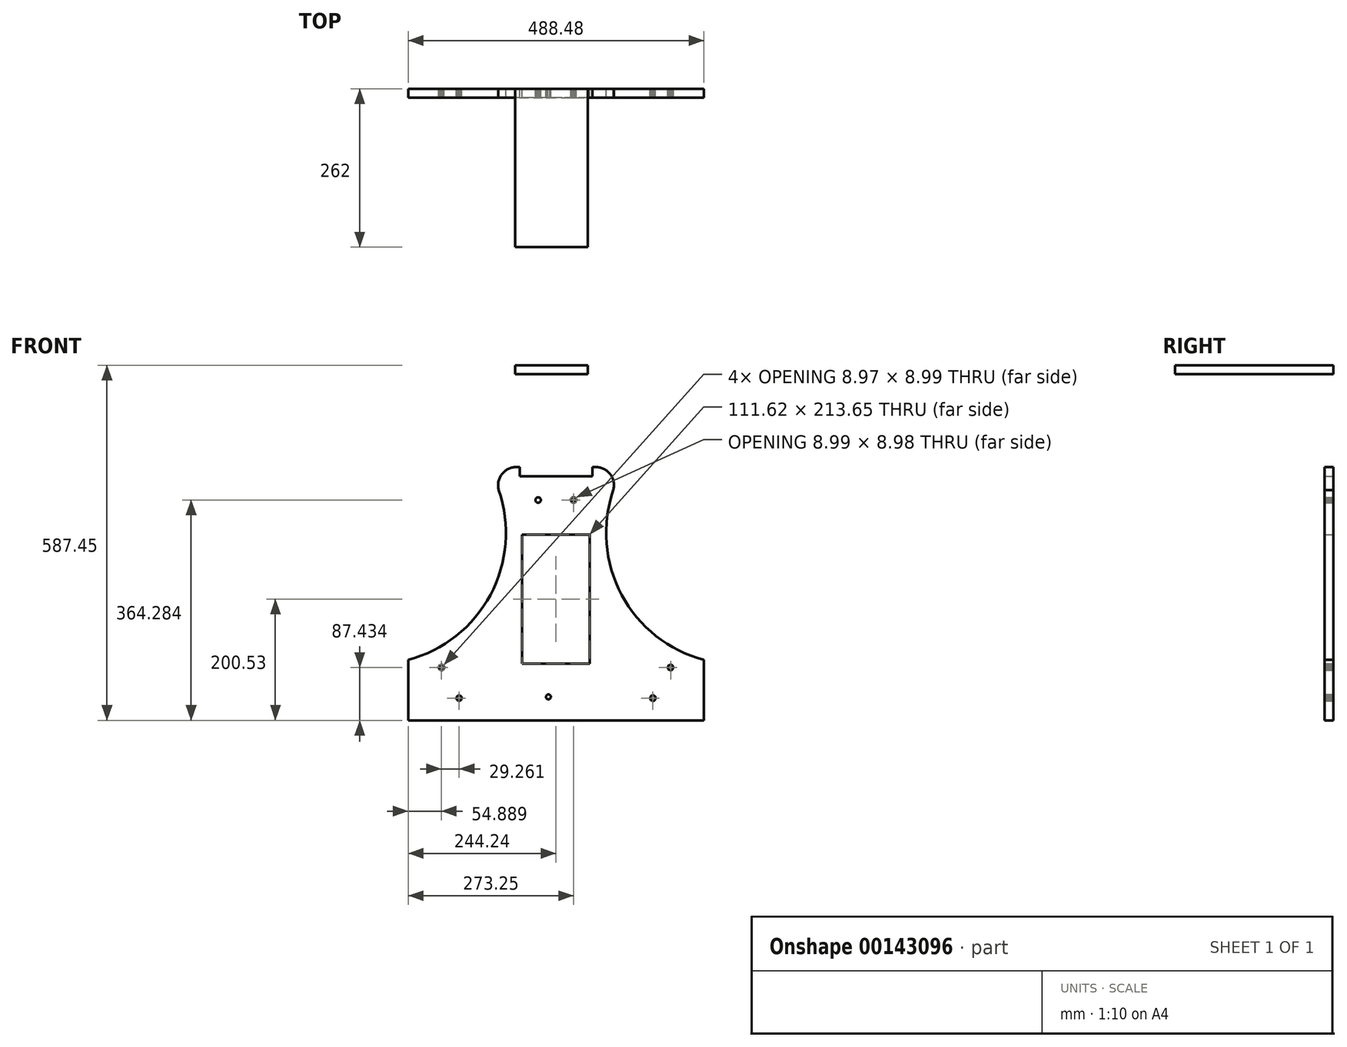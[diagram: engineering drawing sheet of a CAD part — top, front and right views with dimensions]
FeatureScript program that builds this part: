
annotation { "Feature Type Name" : "Feature", "Feature Type Description" : "" }
export const myFeature = defineFeature(function(context is Context, id is Id, definition is map)
    precondition{}
    {
        {
            var Q0;
            Q0=qCreatedBy(makeId("Front.planeOp"),FACE);
            var sketch = newSketch(context, id + "F0", { "sketchPlane" : qUnion([Q0])});
            skLineSegment(sketch, "E0", {"start": v(-16.38, -155.1) * mm, "end": v(-13.24, -155.1) * mm});
            skLineSegment(sketch, "E1", {"start": v(-13.24, -155.1) * mm, "end": v(-12.29, -155.09) * mm});
            skLineSegment(sketch, "E2", {"start": v(-12.29, -155.09) * mm, "end": v(-12.29, -155.23) * mm});
            skLineSegment(sketch, "E3", {"start": v(-12.29, -155.23) * mm, "end": v(-15.24, -155.23) * mm});
            skLineSegment(sketch, "E4", {"start": v(-15.24, -155.23) * mm, "end": v(-15.24, -158.33) * mm});
            skLineSegment(sketch, "E5", {"start": v(-15.24, -158.33) * mm, "end": v(-15.86, -159) * mm});
            skLineSegment(sketch, "E6", {"start": v(-15.86, -159) * mm, "end": v(-16.32, -159.79) * mm});
            skLineSegment(sketch, "E7", {"start": v(-16.32, -159.79) * mm, "end": v(-16.6, -160.66) * mm});
            skLineSegment(sketch, "E8", {"start": v(-16.6, -160.66) * mm, "end": v(-16.69, -161.56) * mm});
            skLineSegment(sketch, "E9", {"start": v(-16.69, -161.56) * mm, "end": v(-16.58, -162.47) * mm});
            skLineSegment(sketch, "E10", {"start": v(-16.58, -162.47) * mm, "end": v(-16.27, -163.33) * mm});
            skLineSegment(sketch, "E11", {"start": v(-16.27, -163.33) * mm, "end": v(-15.79, -164.1) * mm});
            skLineSegment(sketch, "E12", {"start": v(-15.79, -164.1) * mm, "end": v(-15.15, -164.75) * mm});
            skLineSegment(sketch, "E13", {"start": v(-15.15, -164.75) * mm, "end": v(-14.39, -165.25) * mm});
            skLineSegment(sketch, "E14", {"start": v(-14.39, -165.25) * mm, "end": v(-13.54, -165.57) * mm});
            skLineSegment(sketch, "E15", {"start": v(-13.54, -165.57) * mm, "end": v(-12.63, -165.7) * mm});
            skLineSegment(sketch, "E16", {"start": v(-12.63, -165.7) * mm, "end": v(-11.72, -165.64) * mm});
            skLineSegment(sketch, "E17", {"start": v(-11.72, -165.64) * mm, "end": v(-10.85, -165.37) * mm});
            skLineSegment(sketch, "E18", {"start": v(-10.85, -165.37) * mm, "end": v(-10.05, -164.93) * mm});
            skLineSegment(sketch, "E19", {"start": v(-10.05, -164.93) * mm, "end": v(-9.37, -164.32) * mm});
            skLineSegment(sketch, "E20", {"start": v(-9.37, -164.32) * mm, "end": v(-8.84, -163.59) * mm});
            skLineSegment(sketch, "E21", {"start": v(-8.84, -163.59) * mm, "end": v(-8.48, -162.75) * mm});
            skLineSegment(sketch, "E22", {"start": v(-8.48, -162.75) * mm, "end": v(-8.3, -161.85) * mm});
            skLineSegment(sketch, "E23", {"start": v(-8.3, -161.85) * mm, "end": v(-8.33, -160.94) * mm});
            skLineSegment(sketch, "E24", {"start": v(-8.33, -160.94) * mm, "end": v(-8.55, -160.06) * mm});
            skLineSegment(sketch, "E25", {"start": v(-8.55, -160.06) * mm, "end": v(-8.95, -159.24) * mm});
            skLineSegment(sketch, "E26", {"start": v(-8.95, -159.24) * mm, "end": v(-9.53, -158.53) * mm});
            skLineSegment(sketch, "E27", {"start": v(-9.53, -158.53) * mm, "end": v(-10.24, -157.96) * mm});
            skLineSegment(sketch, "E28", {"start": v(-10.24, -157.96) * mm, "end": v(-10.24, -155.1) * mm});
            skLineSegment(sketch, "E29", {"start": v(-10.24, -155.1) * mm, "end": v(-6.14, -155.1) * mm});
            skLineSegment(sketch, "E30", {"start": v(-161.28, -168.1) * mm, "end": v(-160.32, -168.25) * mm});
            skLineSegment(sketch, "E31", {"start": v(-160.32, -168.25) * mm, "end": v(-159.35, -168.2) * mm});
            skLineSegment(sketch, "E32", {"start": v(-159.35, -168.2) * mm, "end": v(-158.41, -167.94) * mm});
            skLineSegment(sketch, "E33", {"start": v(-158.41, -167.94) * mm, "end": v(-158.38, -167.92) * mm});
            skLineSegment(sketch, "E34", {"start": v(-158.38, -167.92) * mm, "end": v(-157.55, -167.48) * mm});
            skLineSegment(sketch, "E35", {"start": v(-157.55, -167.48) * mm, "end": v(-156.8, -166.85) * mm});
            skLineSegment(sketch, "E36", {"start": v(-156.8, -166.85) * mm, "end": v(-156.22, -166.08) * mm});
            skLineSegment(sketch, "E37", {"start": v(-156.22, -166.08) * mm, "end": v(-155.81, -165.2) * mm});
            skLineSegment(sketch, "E38", {"start": v(-155.81, -165.2) * mm, "end": v(-155.6, -164.24) * mm});
            skLineSegment(sketch, "E39", {"start": v(-155.6, -164.24) * mm, "end": v(-155.6, -163.27) * mm});
            skLineSegment(sketch, "E40", {"start": v(-155.6, -163.27) * mm, "end": v(-155.81, -162.32) * mm});
            skLineSegment(sketch, "E41", {"start": v(-155.81, -162.32) * mm, "end": v(-156.22, -161.44) * mm});
            skLineSegment(sketch, "E42", {"start": v(-156.22, -161.44) * mm, "end": v(-156.8, -160.66) * mm});
            skLineSegment(sketch, "E43", {"start": v(-156.8, -160.66) * mm, "end": v(-157.55, -160.03) * mm});
            skLineSegment(sketch, "E44", {"start": v(-157.55, -160.03) * mm, "end": v(-158.41, -159.58) * mm});
            skLineSegment(sketch, "E45", {"start": v(-158.41, -159.58) * mm, "end": v(-159.35, -159.32) * mm});
            skLineSegment(sketch, "E46", {"start": v(-159.35, -159.32) * mm, "end": v(-160.32, -159.26) * mm});
            skLineSegment(sketch, "E47", {"start": v(-160.32, -159.26) * mm, "end": v(-161.28, -159.42) * mm});
            skLineSegment(sketch, "E48", {"start": v(-161.28, -159.42) * mm, "end": v(-162.18, -159.78) * mm});
            skLineSegment(sketch, "E49", {"start": v(-162.18, -159.78) * mm, "end": v(-163, -160.33) * mm});
            skLineSegment(sketch, "E50", {"start": v(-163, -160.33) * mm, "end": v(-163.66, -161.04) * mm});
            skLineSegment(sketch, "E51", {"start": v(-163.66, -161.04) * mm, "end": v(-164.16, -161.87) * mm});
            skLineSegment(sketch, "E52", {"start": v(-164.16, -161.87) * mm, "end": v(-164.47, -162.8) * mm});
            skLineSegment(sketch, "E53", {"start": v(-164.47, -162.8) * mm, "end": v(-164.58, -163.76) * mm});
            skLineSegment(sketch, "E54", {"start": v(-164.58, -163.76) * mm, "end": v(-164.47, -164.73) * mm});
            skLineSegment(sketch, "E55", {"start": v(-164.47, -164.73) * mm, "end": v(-164.16, -165.65) * mm});
            skLineSegment(sketch, "E56", {"start": v(-164.16, -165.65) * mm, "end": v(-163.66, -166.48) * mm});
            skLineSegment(sketch, "E57", {"start": v(-163.66, -166.48) * mm, "end": v(-163, -167.19) * mm});
            skLineSegment(sketch, "E58", {"start": v(-163, -167.19) * mm, "end": v(-162.18, -167.73) * mm});
            skLineSegment(sketch, "E59", {"start": v(-162.18, -167.73) * mm, "end": v(-161.28, -168.1) * mm});
            skLineSegment(sketch, "E60", {"start": v(185.48, -115.42) * mm, "end": v(186.07, -116.2) * mm});
            skLineSegment(sketch, "E61", {"start": v(186.07, -116.2) * mm, "end": v(186.81, -116.82) * mm});
            skLineSegment(sketch, "E62", {"start": v(186.81, -116.82) * mm, "end": v(187.67, -117.28) * mm});
            skLineSegment(sketch, "E63", {"start": v(187.67, -117.28) * mm, "end": v(188.6, -117.54) * mm});
            skLineSegment(sketch, "E64", {"start": v(188.6, -117.54) * mm, "end": v(189.58, -117.59) * mm});
            skLineSegment(sketch, "E65", {"start": v(189.58, -117.59) * mm, "end": v(190.54, -117.43) * mm});
            skLineSegment(sketch, "E66", {"start": v(190.54, -117.43) * mm, "end": v(191.45, -117.07) * mm});
            skLineSegment(sketch, "E67", {"start": v(191.45, -117.07) * mm, "end": v(192.25, -116.53) * mm});
            skLineSegment(sketch, "E68", {"start": v(192.25, -116.53) * mm, "end": v(192.92, -115.82) * mm});
            skLineSegment(sketch, "E69", {"start": v(192.92, -115.82) * mm, "end": v(193.42, -114.99) * mm});
            skLineSegment(sketch, "E70", {"start": v(193.42, -114.99) * mm, "end": v(193.73, -114.06) * mm});
            skLineSegment(sketch, "E71", {"start": v(193.73, -114.06) * mm, "end": v(193.84, -113.1) * mm});
            skLineSegment(sketch, "E72", {"start": v(193.84, -113.1) * mm, "end": v(193.73, -112.13) * mm});
            skLineSegment(sketch, "E73", {"start": v(193.73, -112.13) * mm, "end": v(193.42, -111.2) * mm});
            skLineSegment(sketch, "E74", {"start": v(193.42, -111.2) * mm, "end": v(192.92, -110.37) * mm});
            skLineSegment(sketch, "E75", {"start": v(192.92, -110.37) * mm, "end": v(192.25, -109.67) * mm});
            skLineSegment(sketch, "E76", {"start": v(192.25, -109.67) * mm, "end": v(191.45, -109.12) * mm});
            skLineSegment(sketch, "E77", {"start": v(191.45, -109.12) * mm, "end": v(190.54, -108.76) * mm});
            skLineSegment(sketch, "E78", {"start": v(190.54, -108.76) * mm, "end": v(189.58, -108.6) * mm});
            skLineSegment(sketch, "E79", {"start": v(189.58, -108.6) * mm, "end": v(188.6, -108.65) * mm});
            skLineSegment(sketch, "E80", {"start": v(188.6, -108.65) * mm, "end": v(187.67, -108.92) * mm});
            skLineSegment(sketch, "E81", {"start": v(187.67, -108.92) * mm, "end": v(186.81, -109.37) * mm});
            skLineSegment(sketch, "E82", {"start": v(186.81, -109.37) * mm, "end": v(186.07, -110) * mm});
            skLineSegment(sketch, "E83", {"start": v(186.07, -110) * mm, "end": v(185.48, -110.78) * mm});
            skLineSegment(sketch, "E84", {"start": v(185.48, -110.78) * mm, "end": v(185.07, -111.66) * mm});
            skLineSegment(sketch, "E85", {"start": v(185.07, -111.66) * mm, "end": v(184.86, -112.6) * mm});
            skLineSegment(sketch, "E86", {"start": v(184.86, -112.6) * mm, "end": v(184.86, -113.58) * mm});
            skLineSegment(sketch, "E87", {"start": v(184.86, -113.58) * mm, "end": v(185.07, -114.53) * mm});
            skLineSegment(sketch, "E88", {"start": v(185.07, -114.53) * mm, "end": v(185.48, -115.42) * mm});
            skLineSegment(sketch, "E89", {"start": v(-30.85, 168.06) * mm, "end": v(-31.74, 167.67) * mm});
            skLineSegment(sketch, "E90", {"start": v(-31.74, 167.67) * mm, "end": v(-32.53, 167.1) * mm});
            skLineSegment(sketch, "E91", {"start": v(-32.53, 167.1) * mm, "end": v(-33.17, 166.36) * mm});
            skLineSegment(sketch, "E92", {"start": v(-33.17, 166.36) * mm, "end": v(-33.64, 165.51) * mm});
            skLineSegment(sketch, "E93", {"start": v(-33.64, 165.51) * mm, "end": v(-33.92, 164.58) * mm});
            skLineSegment(sketch, "E94", {"start": v(-33.92, 164.58) * mm, "end": v(-33.99, 163.6) * mm});
            skLineSegment(sketch, "E95", {"start": v(-33.99, 163.6) * mm, "end": v(-33.85, 162.65) * mm});
            skLineSegment(sketch, "E96", {"start": v(-33.85, 162.65) * mm, "end": v(-33.5, 161.73) * mm});
            skLineSegment(sketch, "E97", {"start": v(-33.5, 161.73) * mm, "end": v(-32.97, 160.92) * mm});
            skLineSegment(sketch, "E98", {"start": v(-32.97, 160.92) * mm, "end": v(-32.28, 160.24) * mm});
            skLineSegment(sketch, "E99", {"start": v(-32.28, 160.24) * mm, "end": v(-31.45, 159.72) * mm});
            skLineSegment(sketch, "E100", {"start": v(-31.45, 159.72) * mm, "end": v(-30.54, 159.4) * mm});
            skLineSegment(sketch, "E101", {"start": v(-30.54, 159.4) * mm, "end": v(-29.57, 159.27) * mm});
            skLineSegment(sketch, "E102", {"start": v(-29.57, 159.27) * mm, "end": v(-28.6, 159.36) * mm});
            skLineSegment(sketch, "E103", {"start": v(-28.6, 159.36) * mm, "end": v(-27.68, 159.65) * mm});
            skLineSegment(sketch, "E104", {"start": v(-27.68, 159.65) * mm, "end": v(-26.83, 160.14) * mm});
            skLineSegment(sketch, "E105", {"start": v(-26.83, 160.14) * mm, "end": v(-26.12, 160.8) * mm});
            skLineSegment(sketch, "E106", {"start": v(-26.12, 160.8) * mm, "end": v(-25.56, 161.6) * mm});
            skLineSegment(sketch, "E107", {"start": v(-25.56, 161.6) * mm, "end": v(-25.18, 162.49) * mm});
            skLineSegment(sketch, "E108", {"start": v(-25.18, 162.49) * mm, "end": v(-25, 163.45) * mm});
            skLineSegment(sketch, "E109", {"start": v(-25, 163.45) * mm, "end": v(-25.04, 164.42) * mm});
            skLineSegment(sketch, "E110", {"start": v(-25.04, 164.42) * mm, "end": v(-25.28, 165.36) * mm});
            skLineSegment(sketch, "E111", {"start": v(-25.28, 165.36) * mm, "end": v(-25.72, 166.23) * mm});
            skLineSegment(sketch, "E112", {"start": v(-25.72, 166.23) * mm, "end": v(-26.34, 166.98) * mm});
            skLineSegment(sketch, "E113", {"start": v(-26.34, 166.98) * mm, "end": v(-27.1, 167.58) * mm});
            skLineSegment(sketch, "E114", {"start": v(-27.1, 167.58) * mm, "end": v(-27.98, 168) * mm});
            skLineSegment(sketch, "E115", {"start": v(-27.98, 168) * mm, "end": v(-28.92, 168.23) * mm});
            skLineSegment(sketch, "E116", {"start": v(-28.92, 168.23) * mm, "end": v(-29.9, 168.25) * mm});
            skLineSegment(sketch, "E117", {"start": v(-29.9, 168.25) * mm, "end": v(-30.85, 168.06) * mm});
            skLineSegment(sketch, "E118", {"start": v(31.02, 159.76) * mm, "end": v(31.67, 160.13) * mm});
            skLineSegment(sketch, "E119", {"start": v(31.67, 160.13) * mm, "end": v(32.4, 160.79) * mm});
            skLineSegment(sketch, "E120", {"start": v(32.4, 160.79) * mm, "end": v(32.95, 161.59) * mm});
            skLineSegment(sketch, "E121", {"start": v(32.95, 161.59) * mm, "end": v(33.33, 162.48) * mm});
            skLineSegment(sketch, "E122", {"start": v(33.33, 162.48) * mm, "end": v(33.5, 163.44) * mm});
            skLineSegment(sketch, "E123", {"start": v(33.5, 163.44) * mm, "end": v(33.47, 164.41) * mm});
            skLineSegment(sketch, "E124", {"start": v(33.47, 164.41) * mm, "end": v(33.22, 165.35) * mm});
            skLineSegment(sketch, "E125", {"start": v(33.22, 165.35) * mm, "end": v(32.78, 166.22) * mm});
            skLineSegment(sketch, "E126", {"start": v(32.78, 166.22) * mm, "end": v(32.17, 166.97) * mm});
            skLineSegment(sketch, "E127", {"start": v(32.17, 166.97) * mm, "end": v(31.4, 167.58) * mm});
            skLineSegment(sketch, "E128", {"start": v(31.4, 167.58) * mm, "end": v(30.53, 168) * mm});
            skLineSegment(sketch, "E129", {"start": v(30.53, 168) * mm, "end": v(29.58, 168.23) * mm});
            skLineSegment(sketch, "E130", {"start": v(29.58, 168.23) * mm, "end": v(28.6, 168.24) * mm});
            skLineSegment(sketch, "E131", {"start": v(28.6, 168.24) * mm, "end": v(27.65, 168.05) * mm});
            skLineSegment(sketch, "E132", {"start": v(27.65, 168.05) * mm, "end": v(26.76, 167.66) * mm});
            skLineSegment(sketch, "E133", {"start": v(26.76, 167.66) * mm, "end": v(25.98, 167.09) * mm});
            skLineSegment(sketch, "E134", {"start": v(25.98, 167.09) * mm, "end": v(25.33, 166.36) * mm});
            skLineSegment(sketch, "E135", {"start": v(25.33, 166.36) * mm, "end": v(24.86, 165.5) * mm});
            skLineSegment(sketch, "E136", {"start": v(24.86, 165.5) * mm, "end": v(24.59, 164.57) * mm});
            skLineSegment(sketch, "E137", {"start": v(24.59, 164.57) * mm, "end": v(24.52, 163.6) * mm});
            skLineSegment(sketch, "E138", {"start": v(24.52, 163.6) * mm, "end": v(24.66, 162.64) * mm});
            skLineSegment(sketch, "E139", {"start": v(24.66, 162.64) * mm, "end": v(25, 161.73) * mm});
            skLineSegment(sketch, "E140", {"start": v(25, 161.73) * mm, "end": v(25.53, 160.91) * mm});
            skLineSegment(sketch, "E141", {"start": v(25.53, 160.91) * mm, "end": v(26.23, 160.23) * mm});
            skLineSegment(sketch, "E142", {"start": v(26.23, 160.23) * mm, "end": v(27.05, 159.71) * mm});
            skLineSegment(sketch, "E143", {"start": v(27.05, 159.71) * mm, "end": v(27.97, 159.39) * mm});
            skLineSegment(sketch, "E144", {"start": v(27.97, 159.39) * mm, "end": v(28.93, 159.26) * mm});
            skLineSegment(sketch, "E145", {"start": v(28.93, 159.26) * mm, "end": v(29.9, 159.35) * mm});
            skLineSegment(sketch, "E146", {"start": v(29.9, 159.35) * mm, "end": v(30.83, 159.65) * mm});
            skLineSegment(sketch, "E147", {"start": v(30.83, 159.65) * mm, "end": v(31.02, 159.76) * mm});
            skLineSegment(sketch, "E148", {"start": v(158.41, -159.58) * mm, "end": v(157.55, -160.03) * mm});
            skLineSegment(sketch, "E149", {"start": v(157.55, -160.03) * mm, "end": v(156.8, -160.66) * mm});
            skLineSegment(sketch, "E150", {"start": v(156.8, -160.66) * mm, "end": v(156.22, -161.44) * mm});
            skLineSegment(sketch, "E151", {"start": v(156.22, -161.44) * mm, "end": v(155.81, -162.32) * mm});
            skLineSegment(sketch, "E152", {"start": v(155.81, -162.32) * mm, "end": v(155.6, -163.27) * mm});
            skLineSegment(sketch, "E153", {"start": v(155.6, -163.27) * mm, "end": v(155.6, -164.24) * mm});
            skLineSegment(sketch, "E154", {"start": v(155.6, -164.24) * mm, "end": v(155.81, -165.2) * mm});
            skLineSegment(sketch, "E155", {"start": v(155.81, -165.2) * mm, "end": v(156.22, -166.08) * mm});
            skLineSegment(sketch, "E156", {"start": v(156.22, -166.08) * mm, "end": v(156.8, -166.85) * mm});
            skLineSegment(sketch, "E157", {"start": v(156.8, -166.85) * mm, "end": v(157.55, -167.48) * mm});
            skLineSegment(sketch, "E158", {"start": v(157.55, -167.48) * mm, "end": v(158.41, -167.94) * mm});
            skLineSegment(sketch, "E159", {"start": v(158.41, -167.94) * mm, "end": v(159.35, -168.2) * mm});
            skLineSegment(sketch, "E160", {"start": v(159.35, -168.2) * mm, "end": v(160.32, -168.25) * mm});
            skLineSegment(sketch, "E161", {"start": v(160.32, -168.25) * mm, "end": v(161.28, -168.1) * mm});
            skLineSegment(sketch, "E162", {"start": v(161.28, -168.1) * mm, "end": v(162.18, -167.73) * mm});
            skLineSegment(sketch, "E163", {"start": v(162.18, -167.73) * mm, "end": v(163, -167.19) * mm});
            skLineSegment(sketch, "E164", {"start": v(163, -167.19) * mm, "end": v(163.66, -166.48) * mm});
            skLineSegment(sketch, "E165", {"start": v(163.66, -166.48) * mm, "end": v(164.16, -165.65) * mm});
            skLineSegment(sketch, "E166", {"start": v(164.16, -165.65) * mm, "end": v(164.47, -164.73) * mm});
            skLineSegment(sketch, "E167", {"start": v(164.47, -164.73) * mm, "end": v(164.58, -163.76) * mm});
            skLineSegment(sketch, "E168", {"start": v(164.58, -163.76) * mm, "end": v(164.47, -162.8) * mm});
            skLineSegment(sketch, "E169", {"start": v(164.47, -162.8) * mm, "end": v(164.16, -161.87) * mm});
            skLineSegment(sketch, "E170", {"start": v(164.16, -161.87) * mm, "end": v(163.66, -161.04) * mm});
            skLineSegment(sketch, "E171", {"start": v(163.66, -161.04) * mm, "end": v(163, -160.33) * mm});
            skLineSegment(sketch, "E172", {"start": v(163, -160.33) * mm, "end": v(162.18, -159.78) * mm});
            skLineSegment(sketch, "E173", {"start": v(162.18, -159.78) * mm, "end": v(162.05, -159.73) * mm});
            skLineSegment(sketch, "E174", {"start": v(162.05, -159.73) * mm, "end": v(161.28, -159.42) * mm});
            skLineSegment(sketch, "E175", {"start": v(161.28, -159.42) * mm, "end": v(160.32, -159.26) * mm});
            skLineSegment(sketch, "E176", {"start": v(160.32, -159.26) * mm, "end": v(159.35, -159.32) * mm});
            skLineSegment(sketch, "E177", {"start": v(159.35, -159.32) * mm, "end": v(158.41, -159.58) * mm});
            skLineSegment(sketch, "E178", {"start": v(-191.45, -109.12) * mm, "end": v(-190.54, -108.76) * mm});
            skLineSegment(sketch, "E179", {"start": v(-190.54, -108.76) * mm, "end": v(-189.58, -108.6) * mm});
            skLineSegment(sketch, "E180", {"start": v(-189.58, -108.6) * mm, "end": v(-188.6, -108.65) * mm});
            skLineSegment(sketch, "E181", {"start": v(-188.6, -108.65) * mm, "end": v(-187.67, -108.92) * mm});
            skLineSegment(sketch, "E182", {"start": v(-187.67, -108.92) * mm, "end": v(-186.81, -109.37) * mm});
            skLineSegment(sketch, "E183", {"start": v(-186.81, -109.37) * mm, "end": v(-186.07, -110) * mm});
            skLineSegment(sketch, "E184", {"start": v(-186.07, -110) * mm, "end": v(-185.48, -110.78) * mm});
            skLineSegment(sketch, "E185", {"start": v(-185.48, -110.78) * mm, "end": v(-185.07, -111.66) * mm});
            skLineSegment(sketch, "E186", {"start": v(-185.07, -111.66) * mm, "end": v(-184.86, -112.6) * mm});
            skLineSegment(sketch, "E187", {"start": v(-184.86, -112.6) * mm, "end": v(-184.86, -113.58) * mm});
            skLineSegment(sketch, "E188", {"start": v(-184.86, -113.58) * mm, "end": v(-185.07, -114.53) * mm});
            skLineSegment(sketch, "E189", {"start": v(-185.07, -114.53) * mm, "end": v(-185.48, -115.42) * mm});
            skLineSegment(sketch, "E190", {"start": v(-185.48, -115.42) * mm, "end": v(-186.07, -116.2) * mm});
            skLineSegment(sketch, "E191", {"start": v(-186.07, -116.2) * mm, "end": v(-186.81, -116.82) * mm});
            skLineSegment(sketch, "E192", {"start": v(-186.81, -116.82) * mm, "end": v(-187.67, -117.28) * mm});
            skLineSegment(sketch, "E193", {"start": v(-187.67, -117.28) * mm, "end": v(-188.6, -117.54) * mm});
            skLineSegment(sketch, "E194", {"start": v(-188.6, -117.54) * mm, "end": v(-189.58, -117.59) * mm});
            skLineSegment(sketch, "E195", {"start": v(-189.58, -117.59) * mm, "end": v(-190.54, -117.43) * mm});
            skLineSegment(sketch, "E196", {"start": v(-190.54, -117.43) * mm, "end": v(-191.45, -117.07) * mm});
            skLineSegment(sketch, "E197", {"start": v(-191.45, -117.07) * mm, "end": v(-192.25, -116.53) * mm});
            skLineSegment(sketch, "E198", {"start": v(-192.25, -116.53) * mm, "end": v(-192.92, -115.82) * mm});
            skLineSegment(sketch, "E199", {"start": v(-192.92, -115.82) * mm, "end": v(-193.42, -114.99) * mm});
            skLineSegment(sketch, "E200", {"start": v(-193.42, -114.99) * mm, "end": v(-193.73, -114.06) * mm});
            skLineSegment(sketch, "E201", {"start": v(-193.73, -114.06) * mm, "end": v(-193.84, -113.1) * mm});
            skLineSegment(sketch, "E202", {"start": v(-193.84, -113.1) * mm, "end": v(-193.73, -112.13) * mm});
            skLineSegment(sketch, "E203", {"start": v(-193.73, -112.13) * mm, "end": v(-193.42, -111.2) * mm});
            skLineSegment(sketch, "E204", {"start": v(-193.42, -111.2) * mm, "end": v(-192.92, -110.37) * mm});
            skLineSegment(sketch, "E205", {"start": v(-192.92, -110.37) * mm, "end": v(-192.25, -109.67) * mm});
            skLineSegment(sketch, "E206", {"start": v(-192.25, -109.67) * mm, "end": v(-191.45, -109.12) * mm});
            skPoint(sketch, "E207.0.midPoint", {"position": v(0, -217.95) * mm});
            skPoint(sketch, "E208.0.midPoint", {"position": v(-2.55, -200.53) * mm});
            skArc(sketch, "E209", {"start": v(169.24, -200.53) * mm, "mid": v(221.89, -170.2) * mm, "end": v(222.08, -109.45) * mm});
            skArc(sketch, "E210.MirrorCS", {"start": v(-169.24, -200.53) * mm, "mid": v(-221.89, -170.2) * mm, "end": v(-222.08, -109.45) * mm});
            skLineSegment(sketch, "E211", {"start": v(-169.24, -200.53) * mm, "end": v(169.24, -200.53) * mm});
            skArc(sketch, "E212", {"start": v(51.9, 188.15) * mm, "mid": v(0, 218.27) * mm, "end": v(-51.9, 188.15) * mm});
            skLineSegment(sketch, "E213.bottom", {"start": v(55.8, 106.83) * mm, "end": v(-55.8, 106.83) * mm});
            skLineSegment(sketch, "E213.top", {"start": v(60.8, -106.83) * mm, "end": v(-60.8, -106.83) * mm});
            skLineSegment(sketch, "E213.left", {"start": v(60.8, 106.83) * mm, "end": v(60.8, -106.83) * mm});
            skLineSegment(sketch, "E213.right", {"start": v(-60.8, 106.83) * mm, "end": v(-60.8, -106.83) * mm});
            skPoint(sketch, "E213.middle", {"position": v(0, 0) * mm});
            skLineSegment(sketch, "E214", {"start": v(-55.8, 106.83) * mm, "end": v(-55.8, -106.83) * mm});
            skLineSegment(sketch, "E215", {"start": v(55.8, 106.83) * mm, "end": v(55.8, -106.83) * mm});
            skLineSegment(sketch, "E216.bottom", {"start": v(60, 218.28) * mm, "end": v(-60, 218.28) * mm});
            skLineSegment(sketch, "E216.top", {"start": v(60, 203.28) * mm, "end": v(-60, 203.28) * mm});
            skLineSegment(sketch, "E216.left", {"start": v(60, 218.28) * mm, "end": v(60, 203.28) * mm});
            skLineSegment(sketch, "E216.right", {"start": v(-60, 218.28) * mm, "end": v(-60, 203.28) * mm});
            skPoint(sketch, "E216.middle", {"position": v(0, 210.78) * mm});
            skLineSegment(sketch, "E217", {"start": v(0, 106.83) * mm, "end": v(0, -106.83) * mm, "construction": true});
            skLineSegment(sketch, "E218.1.0", {"start": v(161.97, -180.84) * mm, "end": v(221.89, -76.87) * mm, "construction": true});
            skLineSegment(sketch, "E218.1.1", {"start": v(234.88, -84.36) * mm, "end": v(221.89, -76.87) * mm, "construction": true});
            skLineSegment(sketch, "E218.1.2", {"start": v(174.96, -188.33) * mm, "end": v(234.88, -84.36) * mm, "construction": true});
            skLineSegment(sketch, "E218.1.3", {"start": v(174.96, -188.33) * mm, "end": v(161.97, -180.84) * mm, "construction": true});
            skLineSegment(sketch, "E218.2.0", {"start": v(-221.75, -77.38) * mm, "end": v(-161.6, -181.21) * mm, "construction": true});
            skLineSegment(sketch, "E218.2.1", {"start": v(-174.57, -188.73) * mm, "end": v(-161.6, -181.21) * mm, "construction": true});
            skLineSegment(sketch, "E218.2.2", {"start": v(-234.73, -84.9) * mm, "end": v(-174.57, -188.73) * mm, "construction": true});
            skLineSegment(sketch, "E218.2.3", {"start": v(-234.73, -84.9) * mm, "end": v(-221.75, -77.38) * mm, "construction": true});
            skPoint(sketch, "E218.center", {"position": v(0, -18.24) * mm});
            skLineSegment(sketch, "E218.anchor1", {"start": v(0, -18.24) * mm, "end": v(-60, 203.28) * mm, "construction": true});
            skLineSegment(sketch, "E218.anchor2", {"start": v(0, -18.24) * mm, "end": v(-161.6, -181.21) * mm, "construction": true});
            skLineSegment(sketch, "E219.bottom", {"start": v(-67.69, 371.92) * mm, "end": v(52.31, 371.92) * mm});
            skLineSegment(sketch, "E219.top", {"start": v(-67.69, 386.92) * mm, "end": v(52.31, 386.92) * mm});
            skLineSegment(sketch, "E219.left", {"start": v(-67.69, 371.92) * mm, "end": v(-67.69, 386.92) * mm});
            skLineSegment(sketch, "E219.right", {"start": v(52.31, 371.92) * mm, "end": v(52.31, 386.92) * mm});
            skLineSegment(sketch, "E220", {"start": v(-16.58, -162.47) * mm, "end": v(-8.33, -160.94) * mm});
            skCircle(sketch, "E221", {"center": v(-12.45, -161.7) * mm, "radius": 4.01 * mm});
            skLineSegment(sketch, "E222", {"start": v(0, 218.27) * mm, "end": v(109.24, 218.27) * mm});
            skLineSegment(sketch, "E223", {"start": v(259.24, 68.27) * mm, "end": v(259.24, -200.53) * mm});
            skLineSegment(sketch, "E224", {"start": v(259.24, -200.53) * mm, "end": v(169.24, -200.53) * mm});
            skLineSegment(sketch, "E225.MirrorCS", {"start": v(-259.24, 68.27) * mm, "end": v(-259.24, -200.53) * mm});
            skLineSegment(sketch, "E226.MirrorCS", {"start": v(0, 218.27) * mm, "end": v(-65.73, 218.27) * mm});
            skLineSegment(sketch, "E227.MirrorCS", {"start": v(-259.24, -200.53) * mm, "end": v(-169.24, -200.53) * mm});
            skPoint(sketch, "E228.visualSharp", {"position": v(259.24, 218.27) * mm});
            skArc(sketch, "E228.filletArc", {"start": v(259.24, 68.27) * mm, "mid": v(215.3, 174.33) * mm, "end": v(109.24, 218.27) * mm});
            skPoint(sketch, "E229.visualSharp", {"position": v(-259.24, 218.27) * mm});
            skArc(sketch, "E229.filletArc", {"start": v(-109.24, 218.27) * mm, "mid": v(-215.3, 174.33) * mm, "end": v(-259.24, 68.27) * mm});
            skLineSegment(sketch, "E230.bottom", {"start": v(-259.24, -200.53) * mm, "end": v(259.24, -200.53) * mm});
            skLineSegment(sketch, "E230.top", {"start": v(-259.24, -220.53) * mm, "end": v(259.24, -220.53) * mm});
            skLineSegment(sketch, "E230.left", {"start": v(-259.24, -200.53) * mm, "end": v(-259.24, -220.53) * mm});
            skLineSegment(sketch, "E230.right", {"start": v(259.24, -200.53) * mm, "end": v(259.24, -220.53) * mm});
            skLineSegment(sketch, "E231.bottom", {"start": v(-259.24, -200.53) * mm, "end": v(-244.24, -200.53) * mm});
            skLineSegment(sketch, "E232.bottom", {"start": v(-259.24, -220.53) * mm, "end": v(-244.24, -220.53) * mm});
            skLineSegment(sketch, "E232.top", {"start": v(-259.24, -100.53) * mm, "end": v(-244.24, -100.53) * mm});
            skLineSegment(sketch, "E232.left", {"start": v(-259.24, -220.53) * mm, "end": v(-259.24, -100.53) * mm});
            skLineSegment(sketch, "E232.right", {"start": v(-244.24, -220.53) * mm, "end": v(-244.24, -100.53) * mm});
            skPoint(sketch, "E233.visualSharp", {"position": v(-109.24, 218.27) * mm});
            skArc(sketch, "E233.filletArc", {"start": v(-65.73, 218.27) * mm, "mid": v(-89.66, 206.37) * mm, "end": v(-94.6, 180.1) * mm});
            skArc(sketch, "E234", {"start": v(-244.24, -100.53) * mm, "mid": v(-108.35, 7.22) * mm, "end": v(-94.6, 180.1) * mm});
            skArc(sketch, "E235.MirrorCS", {"start": v(65.73, 218.27) * mm, "mid": v(89.66, 206.37) * mm, "end": v(94.6, 180.1) * mm});
            skArc(sketch, "E236.MirrorCS", {"start": v(244.24, -100.53) * mm, "mid": v(108.35, 7.22) * mm, "end": v(94.6, 180.1) * mm});
            skLineSegment(sketch, "E237.MirrorCS", {"start": v(244.24, -220.53) * mm, "end": v(244.24, -100.53) * mm});
            skLineSegment(sketch, "E238.MirrorCS", {"start": v(259.24, -100.53) * mm, "end": v(244.24, -100.53) * mm});
            skSolve(sketch);
        }
        {
            var Q0;
            {var subQ62=sQuery(id+"F0.wireOp",EDGE,"E10");Q0=makeQuery(id+"F0.imprint","IMPRINT",FACE,{"disambiguationData":[TD([[makeQuery(id+"F0.imprint","IMPRINT",EDGE,{"derivedFrom":subQ62}),-1.0]])]});}
            var Q1;
            {var subQ0=sQuery(id+"F0.wireOp",EDGE,"E212");var subQ2=sQuery(id+"F0.wireOp",EDGE,"E216.bottom");var subQ3=makeQuery(id+"F0.imprint","INTERSECT",VERTEX,{"disambiguationData":[OD(0.0)],"derivedFrom":[subQ0,subQ2]});Q1=makeQuery(id+"F0.imprint","IMPRINT",FACE,{"disambiguationData":[TD([[makeQuery(id+"F0.imprint","IMPRINT",EDGE,{"disambiguationData":[TD([[subQ3,-1.0]])],"derivedFrom":subQ2}),-1.0]])]});}
            var Q2;
            {var subQ11=sQuery(id+"F0.wireOp",EDGE,"E53");Q2=makeQuery(id+"F0.imprint","IMPRINT",FACE,{"disambiguationData":[TD([[makeQuery(id+"F0.imprint","IMPRINT",EDGE,{"derivedFrom":subQ11}),-1.0]])]});}
            var Q3;
            {var subQ14=sQuery(id+"F0.wireOp",EDGE,"E66");Q3=makeQuery(id+"F0.imprint","IMPRINT",FACE,{"disambiguationData":[TD([[makeQuery(id+"F0.imprint","IMPRINT",EDGE,{"derivedFrom":subQ14}),-1.0]])]});}
            var Q4;
            Q4=makeQuery(id+"F0.imprint","IMPRINT",FACE,{"disambiguationData":[TD([[makeQuery(id+"F0.imprint","IMPRINT",EDGE,{"derivedFrom":sQuery(id+"F0.wireOp",EDGE,"E218.1.0")}),-1.0]])]});
            var Q5;
            Q5=makeQuery(id+"F0.imprint","IMPRINT",FACE,{"disambiguationData":[TD([[makeQuery(id+"F0.imprint","IMPRINT",EDGE,{"derivedFrom":sQuery(id+"F0.wireOp",EDGE,"E218.2.0")}),-1.0]])]});
            var Q6;
            {var subQ5=sQuery(id+"F0.wireOp",EDGE,"E230.bottom");var subQ6=makeQuery(id+"F0.imprint","IMPRINT",VERTEX,{"disambiguationData":[OD(0.0)],"derivedFrom":subQ5});Q6=makeQuery(id+"F0.imprint","IMPRINT",FACE,{"disambiguationData":[TD([[makeQuery(id+"F0.imprint","IMPRINT",EDGE,{"disambiguationData":[TD([[subQ6,1.0]])],"derivedFrom":subQ5}),-1.0]])]});}
            extrude(context, id + "F1", {"entities" : qUnion([Q0, Q1, Q2, Q3, Q4, Q5, Q6]), "depth" : 15 * mm});
        }
        {
            var Q0;
            Q0=makeQuery(id+"F0.imprint","IMPRINT",FACE,{"disambiguationData":[TD([[makeQuery(id+"F0.imprint","IMPRINT",EDGE,{"derivedFrom":sQuery(id+"F0.wireOp",EDGE,"E219.bottom")}),1.0]])]});
            var Q1;
            {var subQ5=sQuery(id+"F0.wireOp",EDGE,"E230.bottom");var subQ6=makeQuery(id+"F0.imprint","IMPRINT",VERTEX,{"disambiguationData":[OD(0.0)],"derivedFrom":subQ5});Q1=makeQuery(id+"F0.imprint","IMPRINT",FACE,{"disambiguationData":[TD([[makeQuery(id+"F0.imprint","IMPRINT",EDGE,{"disambiguationData":[TD([[subQ6,1.0]])],"derivedFrom":subQ5}),-1.0]])]});}
            extrude(context, id + "F2", {"entities" : qUnion([Q0, Q1]), "depth" : 262 * mm});
        }
    });
